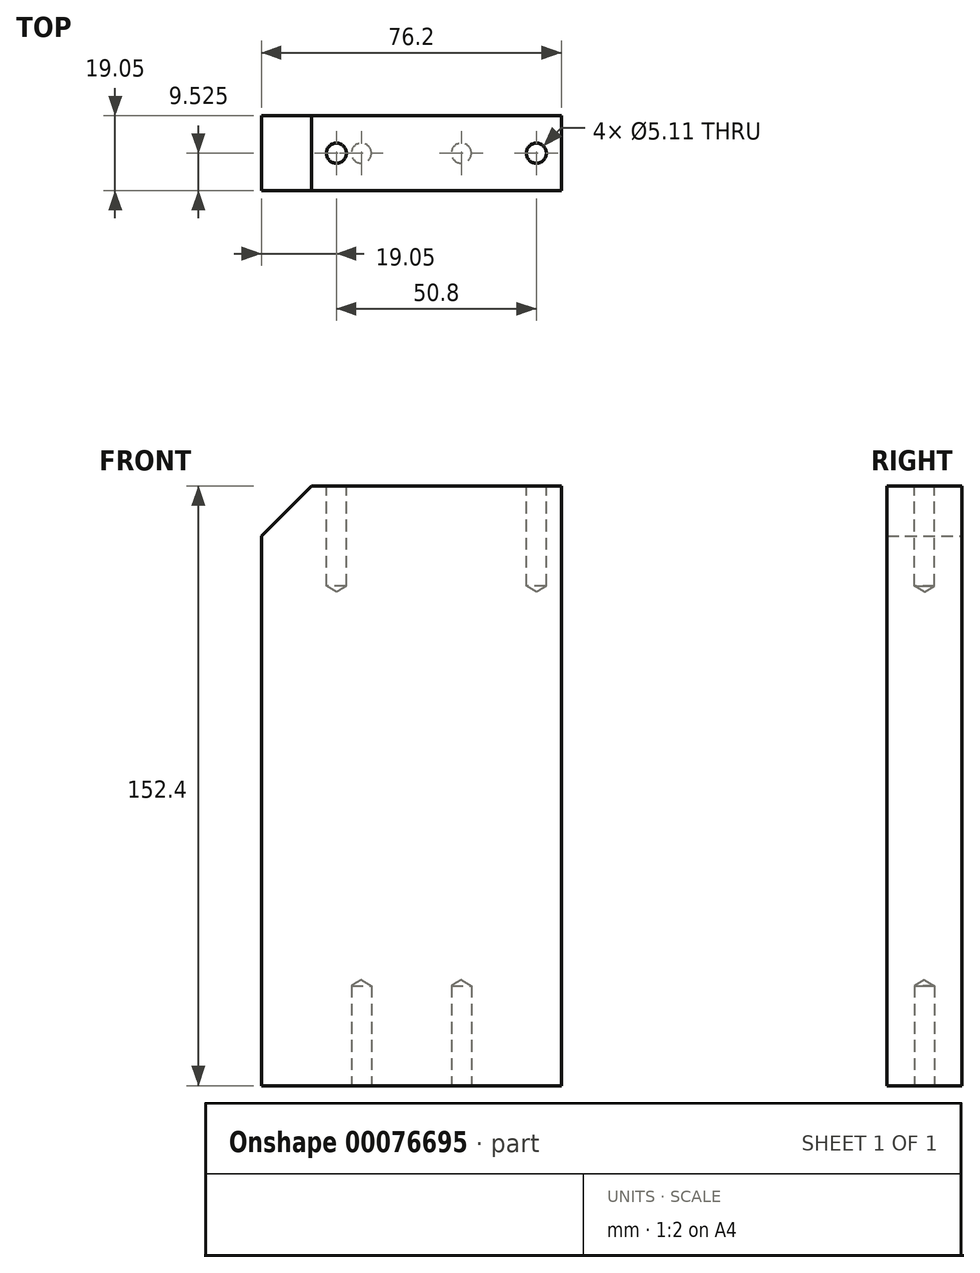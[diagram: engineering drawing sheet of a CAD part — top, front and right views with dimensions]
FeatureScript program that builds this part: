
annotation { "Feature Type Name" : "Feature", "Feature Type Description" : "" }
export const myFeature = defineFeature(function(context is Context, id is Id, definition is map)
    precondition{}
    {
        {
            var Q0;
            Q0=qCreatedBy(makeId("Front.planeOp"),FACE);
            var sketch = newSketch(context, id + "F0", { "sketchPlane" : qUnion([Q0])});
            skLineSegment(sketch, "E0.bottom", {"start": v(-76.2, 152.4) * mm, "end": v(0, 152.4) * mm});
            skLineSegment(sketch, "E0.top", {"start": v(-76.2, 0) * mm, "end": v(0, 0) * mm});
            skLineSegment(sketch, "E0.left", {"start": v(-76.2, 152.4) * mm, "end": v(-76.2, 0) * mm});
            skLineSegment(sketch, "E0.right", {"start": v(0, 152.4) * mm, "end": v(0, 0) * mm});
            skSolve(sketch);
        }
        {
            var Q0;
            Q0=makeQuery(id+"F0.imprint","IMPRINT",FACE,{"disambiguationData":[TD([[makeQuery(id+"F0.imprint","IMPRINT",EDGE,{"derivedFrom":sQuery(id+"F0.wireOp",EDGE,"E0.bottom")}),-1.0]])]});
            extrude(context, id + "F1", {"entities" : qUnion([Q0]), "depth" : 19.05 * mm});
        }
        {
            var Q0;
            Q0=makeQuery(id+"F1.opExtrude","SWEPT_FACE",FACE,{"disambiguationData":[OSD([sQuery(id+"F0.wireOp",EDGE,"E0.top")])]});
            var sketch = newSketch(context, id + "F2", { "sketchPlane" : qUnion([Q0])});
            skLineSegment(sketch, "E1.0", {"start": v(-76.2, 9.53) * mm, "end": v(0, 9.53) * mm, "construction": true});
            skLineSegment(sketch, "E2.0", {"start": v(-50.8, 19.05) * mm, "end": v(-50.8, 0) * mm, "construction": true});
            skLineSegment(sketch, "E3.0", {"start": v(-25.4, 19.05) * mm, "end": v(-25.4, 0) * mm, "construction": true});
            skCircle(sketch, "E4", {"center": v(-50.8, 9.53) * mm, "radius": 2.55 * mm});
            skCircle(sketch, "E5", {"center": v(-25.4, 9.53) * mm, "radius": 2.55 * mm});
            skSolve(sketch);
        }
        {
            var Q0;
            Q0=sQuery(id+"F2.wireOp",VERTEX,"E4.center");
            var Q1;
            Q1=makeQuery(id+"F1.opExtrude","SWEPT_BODY",BODY,{"disambiguationData":[OSD([sQuery(id+"F0.wireOp",EDGE,"E0.bottom"),sQuery(id+"F0.wireOp",EDGE,"E0.top"),sQuery(id+"F0.wireOp",EDGE,"E0.left"),sQuery(id+"F0.wireOp",EDGE,"E0.right")])]});
            hole(context, id + "F3", {"style" : HoleStyle.SIMPLE, "endStyle" : HoleEndStyle.BLIND, "holeDiameter" : 5.1 * mm, "holeDepth" : 25.4 * mm, "locations" : qUnion([Q0]), "scope" : qUnion([Q1])});
        }
        {
            var Q0;
            Q0=sQuery(id+"F2.wireOp",VERTEX,"E5.center");
            var Q1;
            Q1=makeQuery(id+"F1.opExtrude","SWEPT_BODY",BODY,{"disambiguationData":[OSD([sQuery(id+"F0.wireOp",EDGE,"E0.bottom"),sQuery(id+"F0.wireOp",EDGE,"E0.top"),sQuery(id+"F0.wireOp",EDGE,"E0.left"),sQuery(id+"F0.wireOp",EDGE,"E0.right")])]});
            hole(context, id + "F4", {"style" : HoleStyle.SIMPLE, "endStyle" : HoleEndStyle.BLIND, "holeDiameter" : 5.1 * mm, "holeDepth" : 25.4 * mm, "locations" : qUnion([Q0]), "scope" : qUnion([Q1])});
        }
        {
            var Q0;
            Q0=makeQuery(id+"F1.opExtrude","SWEPT_FACE",FACE,{"disambiguationData":[OSD([sQuery(id+"F0.wireOp",EDGE,"E0.bottom")])]});
            var sketch = newSketch(context, id + "F5", { "sketchPlane" : qUnion([Q0])});
            skLineSegment(sketch, "E6.0", {"start": v(-57.15, -19.05) * mm, "end": v(-57.15, 0) * mm, "construction": true});
            skLineSegment(sketch, "E7.0", {"start": v(-6.35, -19.05) * mm, "end": v(-6.35, 0) * mm, "construction": true});
            skCircle(sketch, "E8", {"center": v(-57.15, -9.53) * mm, "radius": 2.55 * mm});
            skCircle(sketch, "E9", {"center": v(-6.35, -9.53) * mm, "radius": 2.55 * mm});
            skSolve(sketch);
        }
        {
            var Q0;
            Q0=sQuery(id+"F5.wireOp",VERTEX,"E8.center");
            var Q1;
            Q1=sQuery(id+"F5.wireOp",VERTEX,"E9.center");
            var Q2;
            Q2=makeQuery(id+"F1.opExtrude","SWEPT_BODY",BODY,{"disambiguationData":[OSD([sQuery(id+"F0.wireOp",EDGE,"E0.bottom"),sQuery(id+"F0.wireOp",EDGE,"E0.top"),sQuery(id+"F0.wireOp",EDGE,"E0.left"),sQuery(id+"F0.wireOp",EDGE,"E0.right")])]});
            hole(context, id + "F6", {"style" : HoleStyle.SIMPLE, "endStyle" : HoleEndStyle.BLIND, "holeDiameter" : 5.1 * mm, "holeDepth" : 25.4 * mm, "locations" : qUnion([Q0, Q1]), "scope" : qUnion([Q2])});
        }
        {
            var Q0;
            Q0=makeQuery(id+"F1.opExtrude","SWEPT_EDGE",EDGE,{"disambiguationData":[OSD([sQuery(id+"F0.wireOp",EDGE,"E0.bottom"),sQuery(id+"F0.wireOp",EDGE,"E0.left")])]});
            chamfer(context, id + "F7", {"entities" : qUnion([Q0]), "width" : 12.7 * mm, "tangentPropagation" : true});
        }
    });
